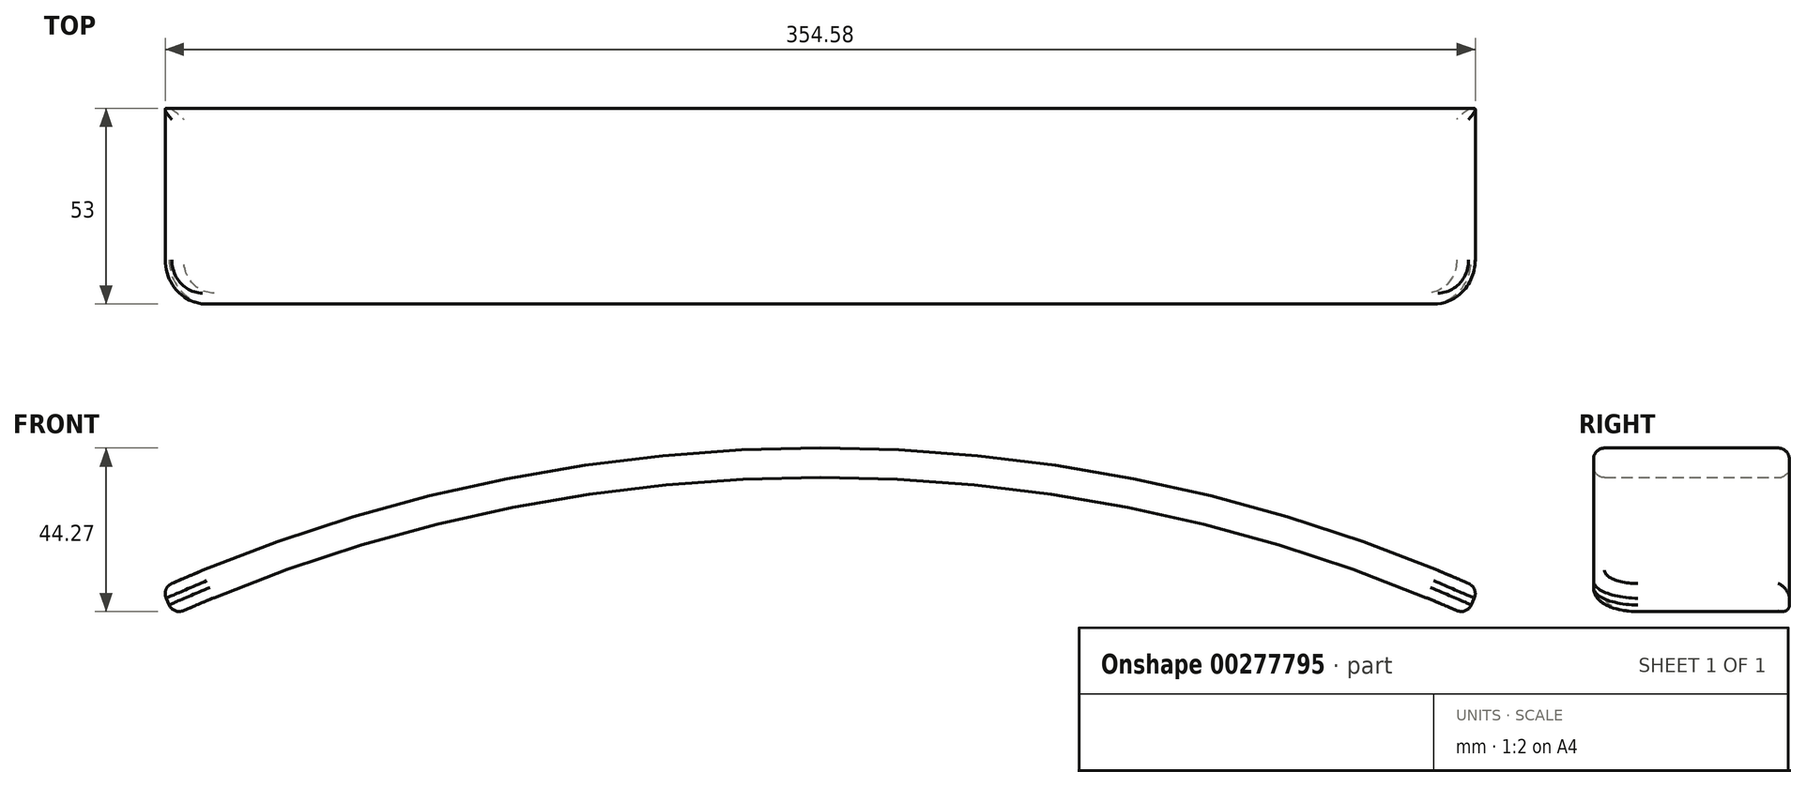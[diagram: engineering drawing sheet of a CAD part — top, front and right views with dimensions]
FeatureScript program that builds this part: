
annotation { "Feature Type Name" : "Feature", "Feature Type Description" : "" }
export const myFeature = defineFeature(function(context is Context, id is Id, definition is map)
    precondition{}
    {
        {
            var Q0;
            Q0=qCreatedBy(makeId("Front.planeOp"),FACE);
            var sketch = newSketch(context, id + "F0", { "sketchPlane" : qUnion([Q0])});
            skArc(sketch, "E0", {"start": v(175, 0) * mm, "mid": v(0, 37.22) * mm, "end": v(-175, 0) * mm});
            skLineSegment(sketch, "E1", {"start": v(-175, 0) * mm, "end": v(175, 0) * mm, "construction": true});
            skArc(sketch, "E2.0", {"start": v(178.26, 7.3) * mm, "mid": v(0, 45.22) * mm, "end": v(-178.26, 7.3) * mm});
            skLineSegment(sketch, "E3", {"start": v(-178.26, 7.3) * mm, "end": v(-175, 0) * mm});
            skLineSegment(sketch, "E4", {"start": v(178.26, 7.3) * mm, "end": v(175, 0) * mm});
            skSolve(sketch);
        }
        {
            var Q0;
            Q0=makeQuery(id+"F0.imprint","IMPRINT",FACE,{"disambiguationData":[TD([[makeQuery(id+"F0.imprint","IMPRINT",EDGE,{"derivedFrom":sQuery(id+"F0.wireOp",EDGE,"E0")}),-1.0]])]});
            extrude(context, id + "F1", {"entities" : qUnion([Q0]), "endBound" : BoundingType.SYMMETRIC, "depth" : 53 * mm});
        }
        {
            var Q0;
            Q0=makeQuery(id+"F1.opExtrude","CAP_EDGE",EDGE,{"disambiguationData":[OSD([sQuery(id+"F0.wireOp",EDGE,"E3")])],"isStart":false});
            var Q1;
            Q1=makeQuery(id+"F1.opExtrude","CAP_EDGE",EDGE,{"disambiguationData":[OSD([sQuery(id+"F0.wireOp",EDGE,"E4")])],"isStart":false});
            fillet(context, id + "F2", {"entities" : qUnion([Q0, Q1]), "radius" : 12 * mm, "tangentPropagation" : true, "allowEdgeOverflow" : false});
        }
        {
            var Q0;
            Q0=makeQuery(id+"F1.opExtrude","SWEPT_FACE",FACE,{"disambiguationData":[OSD([sQuery(id+"F0.wireOp",EDGE,"E0")])]});
            var Q1;
            Q1=makeQuery(id+"F1.opExtrude","SWEPT_FACE",FACE,{"disambiguationData":[OSD([sQuery(id+"F0.wireOp",EDGE,"E2.0")])]});
            fillet(context, id + "F3", {"entities" : qUnion([Q0, Q1]), "radius" : 3 * mm, "tangentPropagation" : true, "allowEdgeOverflow" : false});
        }
    });
